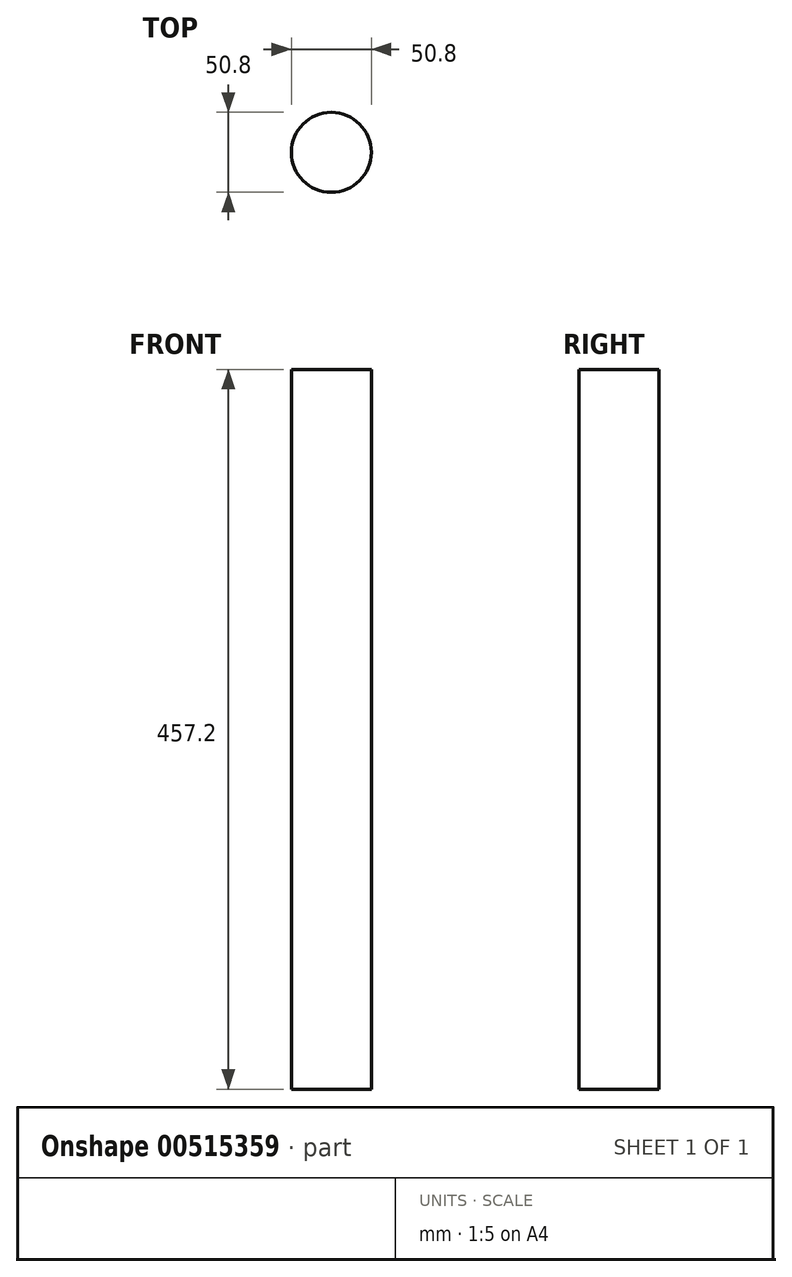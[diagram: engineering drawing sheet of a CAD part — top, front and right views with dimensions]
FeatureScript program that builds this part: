
annotation { "Feature Type Name" : "Feature", "Feature Type Description" : "" }
export const myFeature = defineFeature(function(context is Context, id is Id, definition is map)
    precondition{}
    {
        {
            var Q0;
            Q0=qCreatedBy(makeId("Top.planeOp"),FACE);
            var sketch = newSketch(context, id + "F0", { "sketchPlane" : qUnion([Q0])});
            skCircle(sketch, "E0", {"center": v(0, 0) * mm, "radius": 25.4 * mm});
            skSolve(sketch);
        }
        {
            var Q0;
            Q0=makeQuery(id+"F0.imprint","IMPRINT",FACE,{"disambiguationData":[TD([[makeQuery(id+"F0.imprint","IMPRINT",EDGE,{"derivedFrom":sQuery(id+"F0.wireOp",EDGE,"E0")}),1.0]])]});
            extrude(context, id + "F1", {"entities" : qUnion([Q0]), "depth" : 457.2 * mm, "offsetDistance" : 25.4 * mm});
        }
    });
